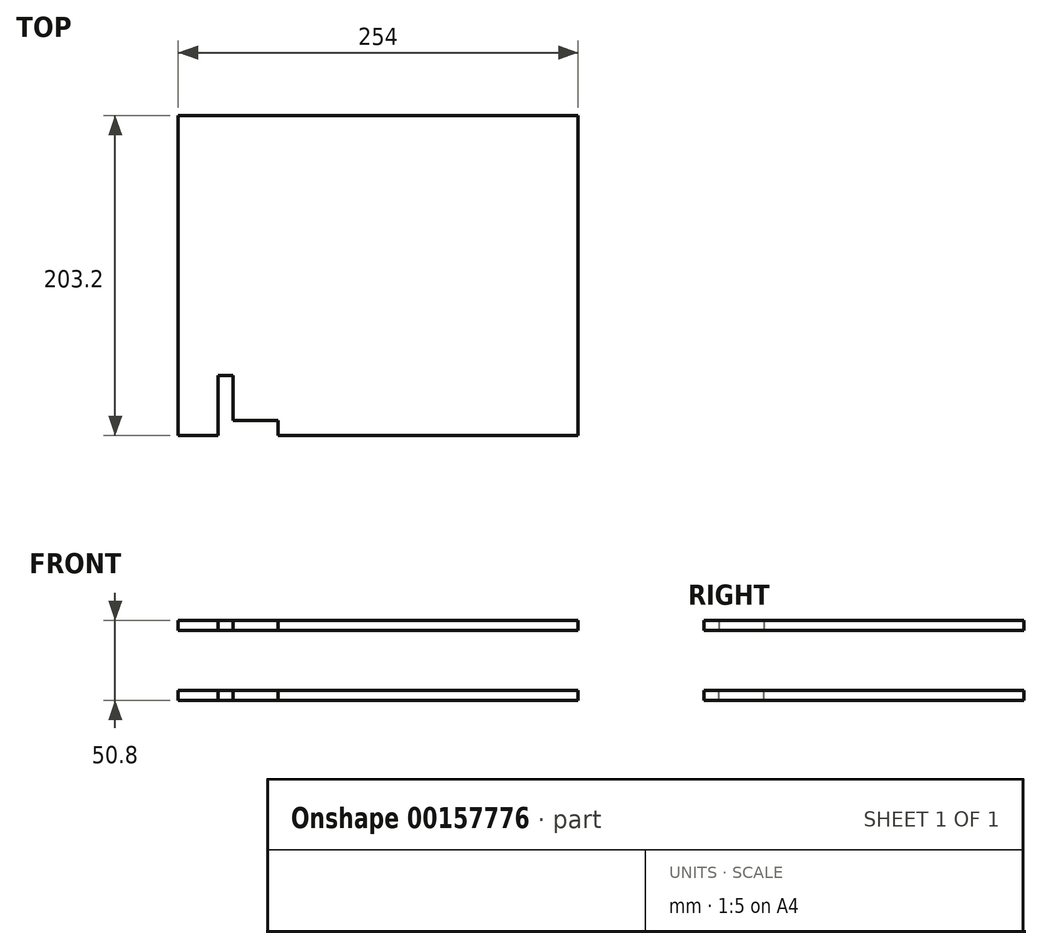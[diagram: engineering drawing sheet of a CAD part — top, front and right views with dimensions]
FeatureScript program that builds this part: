
annotation { "Feature Type Name" : "Feature", "Feature Type Description" : "" }
export const myFeature = defineFeature(function(context is Context, id is Id, definition is map)
    precondition{}
    {
        {
            var Q0;
            Q0=qCreatedBy(makeId("Top.planeOp"),FACE);
            var sketch = newSketch(context, id + "F0", { "sketchPlane" : qUnion([Q0])});
            skLineSegment(sketch, "E0.bottom", {"start": v(127, 101.6) * mm, "end": v(-127, 101.6) * mm});
            skLineSegment(sketch, "E0.top", {"start": v(127, -101.6) * mm, "end": v(-127, -101.6) * mm});
            skLineSegment(sketch, "E0.left", {"start": v(127, 101.6) * mm, "end": v(127, -101.6) * mm});
            skLineSegment(sketch, "E0.right", {"start": v(-127, 101.6) * mm, "end": v(-127, -101.6) * mm});
            skPoint(sketch, "E0.middle", {"position": v(0, 0) * mm});
            skLineSegment(sketch, "E1.bottom", {"start": v(-101.6, -101.6) * mm, "end": v(101.6, -101.6) * mm, "construction": true});
            skLineSegment(sketch, "E1.top", {"start": v(-101.6, 101.6) * mm, "end": v(101.6, 101.6) * mm, "construction": true});
            skLineSegment(sketch, "E1.left", {"start": v(-101.6, -101.6) * mm, "end": v(-101.6, 101.6) * mm, "construction": true});
            skLineSegment(sketch, "E1.right", {"start": v(101.6, -101.6) * mm, "end": v(101.6, 101.6) * mm, "construction": true});
            skLineSegment(sketch, "E2", {"start": v(-101.6, -63.5) * mm, "end": v(-92.08, -63.5) * mm});
            skLineSegment(sketch, "E3", {"start": v(-92.08, -63.5) * mm, "end": v(-92.08, -92.08) * mm});
            skLineSegment(sketch, "E4", {"start": v(-92.08, -92.08) * mm, "end": v(-63.5, -92.08) * mm});
            skLineSegment(sketch, "E5", {"start": v(-63.5, -92.08) * mm, "end": v(-63.5, -101.6) * mm});
            skLineSegment(sketch, "E6", {"start": v(-63.5, -101.6) * mm, "end": v(-101.6, -101.6) * mm});
            skLineSegment(sketch, "E7", {"start": v(-101.6, -101.6) * mm, "end": v(-101.6, -63.5) * mm});
            skSolve(sketch);
        }
        {
            var Q0;
            Q0=makeQuery(id+"F0.imprint","IMPRINT",FACE,{"disambiguationData":[TD([[makeQuery(id+"F0.imprint","IMPRINT",EDGE,{"derivedFrom":sQuery(id+"F0.wireOp",EDGE,"E0.bottom")}),1.0]])]});
            extrude(context, id + "F1", {"entities" : qUnion([Q0]), "depth" : 6.35 * mm});
        }
        {
            var Q0;
            Q0=qCreatedBy(makeId("Top.planeOp"),FACE);
            cPlane(context, id + "F2", {"entities" : qUnion([Q0]), "cplaneType" : CPlaneType.OFFSET, "offset" : 19.05 * mm, "oppositeDirection" : true, "width" : 152.4 * mm, "height" : 152.4 * mm});
        }
        {
            var Q0;
            Q0=makeQuery(id+"F1.opExtrude","SWEPT_BODY",BODY,{"disambiguationData":[OSD([sQuery(id+"F0.wireOp",EDGE,"E0.bottom"),sQuery(id+"F0.wireOp",EDGE,"E0.top"),sQuery(id+"F0.wireOp",EDGE,"E0.left"),sQuery(id+"F0.wireOp",EDGE,"E0.right")])]});
            var Q1;
            Q1=qCreatedBy(id+"F2.planeOp",FACE);
            mirror(context, id + "F3", {"entities" : qUnion([Q0]), "mirrorPlane" : qUnion([Q1])});
        }
    });
